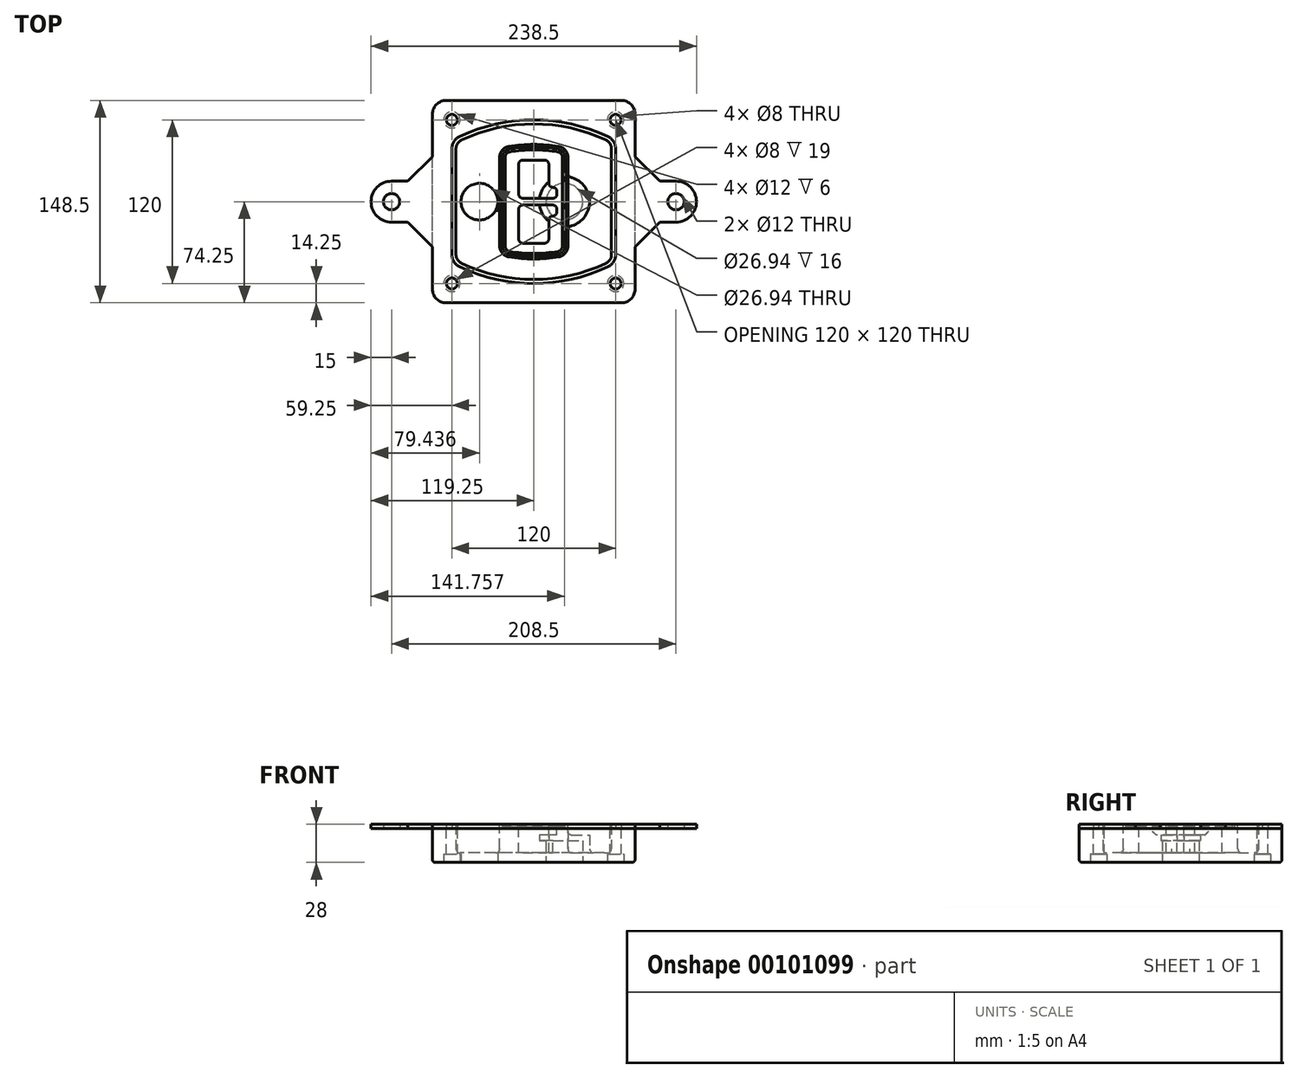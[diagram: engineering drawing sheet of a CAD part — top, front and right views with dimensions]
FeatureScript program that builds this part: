
annotation { "Feature Type Name" : "Feature", "Feature Type Description" : "" }
export const myFeature = defineFeature(function(context is Context, id is Id, definition is map)
    precondition{}
    {
        {
            var Q0;
            Q0=qCreatedBy(makeId("Top.planeOp"),FACE);
            var sketch = newSketch(context, id + "F0", { "sketchPlane" : qUnion([Q0])});
            skPoint(sketch, "E0.rect.middle", {"position": v(0, 0) * mm});
            skLineSegment(sketch, "E1.bottom", {"start": v(-64.25, -74.25) * mm, "end": v(64.25, -74.25) * mm});
            skLineSegment(sketch, "E1.top", {"start": v(-64.25, 74.25) * mm, "end": v(64.25, 74.25) * mm});
            skLineSegment(sketch, "E1.left", {"start": v(-74.25, -64.25) * mm, "end": v(-74.25, 64.25) * mm});
            skLineSegment(sketch, "E1.right", {"start": v(74.25, -64.25) * mm, "end": v(74.25, 64.25) * mm});
            skLineSegment(sketch, "E2", {"start": v(-74.25, 74.25) * mm, "end": v(74.25, -74.25) * mm, "construction": true});
            skLineSegment(sketch, "E3", {"start": v(74.25, 74.25) * mm, "end": v(-74.25, -74.25) * mm, "construction": true});
            skCircle(sketch, "E4", {"center": v(-60, 60) * mm, "radius": 4 * mm});
            skCircle(sketch, "E5", {"center": v(60, 60) * mm, "radius": 4 * mm});
            skCircle(sketch, "E6", {"center": v(60, -60) * mm, "radius": 4 * mm});
            skCircle(sketch, "E7", {"center": v(-60, -60) * mm, "radius": 4 * mm});
            skLineSegment(sketch, "E8", {"start": v(-60, 60) * mm, "end": v(60, 60) * mm, "construction": true});
            skLineSegment(sketch, "E9", {"start": v(60, 60) * mm, "end": v(60, -60) * mm, "construction": true});
            skLineSegment(sketch, "E10", {"start": v(60, -60) * mm, "end": v(-60, -60) * mm, "construction": true});
            skLineSegment(sketch, "E11", {"start": v(-60, -60) * mm, "end": v(-60, 60) * mm, "construction": true});
            skLineSegment(sketch, "E12", {"start": v(-60, 38.83) * mm, "end": v(-60, -38.83) * mm});
            skLineSegment(sketch, "E13", {"start": v(60, 38.83) * mm, "end": v(60, -38.83) * mm});
            skArc(sketch, "E14", {"start": v(54.26, 47.88) * mm, "mid": v(0, 60) * mm, "end": v(-54.26, 47.88) * mm});
            skArc(sketch, "E15", {"start": v(-54.26, -47.88) * mm, "mid": v(0, -60) * mm, "end": v(54.26, -47.88) * mm});
            skLineSegment(sketch, "E16", {"start": v(-60, 0) * mm, "end": v(60, 0) * mm, "construction": true});
            skPoint(sketch, "E17.visualSharp", {"position": v(-60, -45) * mm});
            skArc(sketch, "E17.filletArc", {"start": v(-60, -38.83) * mm, "mid": v(-58.44, -44.2) * mm, "end": v(-54.26, -47.88) * mm});
            skPoint(sketch, "E18.visualSharp", {"position": v(-60, 45) * mm});
            skArc(sketch, "E18.filletArc", {"start": v(-54.26, 47.88) * mm, "mid": v(-58.44, 44.2) * mm, "end": v(-60, 38.83) * mm});
            skPoint(sketch, "E19.visualSharp", {"position": v(60, 45) * mm});
            skArc(sketch, "E19.filletArc", {"start": v(60, 38.83) * mm, "mid": v(58.44, 44.2) * mm, "end": v(54.26, 47.88) * mm});
            skPoint(sketch, "E20.visualSharp", {"position": v(60, -45) * mm});
            skArc(sketch, "E20.filletArc", {"start": v(54.26, -47.88) * mm, "mid": v(58.44, -44.2) * mm, "end": v(60, -38.83) * mm});
            skPoint(sketch, "E21.visualSharp", {"position": v(-74.25, 74.25) * mm});
            skArc(sketch, "E21.filletArc", {"start": v(-64.25, 74.25) * mm, "mid": v(-71.32, 71.32) * mm, "end": v(-74.25, 64.25) * mm});
            skPoint(sketch, "E22.visualSharp", {"position": v(74.25, 74.25) * mm});
            skArc(sketch, "E22.filletArc", {"start": v(74.25, 64.25) * mm, "mid": v(71.32, 71.32) * mm, "end": v(64.25, 74.25) * mm});
            skPoint(sketch, "E23.visualSharp", {"position": v(74.25, -74.25) * mm});
            skArc(sketch, "E23.filletArc", {"start": v(64.25, -74.25) * mm, "mid": v(71.32, -71.32) * mm, "end": v(74.25, -64.25) * mm});
            skPoint(sketch, "E24.visualSharp", {"position": v(-74.25, -74.25) * mm});
            skArc(sketch, "E24.filletArc", {"start": v(-74.25, -64.25) * mm, "mid": v(-71.32, -71.32) * mm, "end": v(-64.25, -74.25) * mm});
            skArc(sketch, "E25.0", {"start": v(57, 38.83) * mm, "mid": v(55.9, 42.58) * mm, "end": v(52.98, 45.17) * mm});
            skLineSegment(sketch, "E25.1", {"start": v(57, 38.83) * mm, "end": v(57, -38.83) * mm});
            skArc(sketch, "E25.2", {"start": v(52.98, -45.17) * mm, "mid": v(55.9, -42.58) * mm, "end": v(57, -38.83) * mm});
            skArc(sketch, "E25.3", {"start": v(-52.98, -45.17) * mm, "mid": v(0, -57) * mm, "end": v(52.98, -45.17) * mm});
            skArc(sketch, "E25.4", {"start": v(-57, -38.83) * mm, "mid": v(-55.9, -42.58) * mm, "end": v(-52.98, -45.17) * mm});
            skArc(sketch, "E25.5", {"start": v(52.98, 45.17) * mm, "mid": v(0, 57) * mm, "end": v(-52.98, 45.17) * mm});
            skLineSegment(sketch, "E25.6", {"start": v(-57, 38.83) * mm, "end": v(-57, -38.83) * mm});
            skArc(sketch, "E25.7", {"start": v(-52.98, 45.17) * mm, "mid": v(-55.9, 42.58) * mm, "end": v(-57, 38.83) * mm});
            skArc(sketch, "E26.0", {"start": v(-55.96, 51.5) * mm, "mid": v(-61.82, 46.33) * mm, "end": v(-64, 38.83) * mm});
            skArc(sketch, "E26.1", {"start": v(55.96, 51.5) * mm, "mid": v(0, 64) * mm, "end": v(-55.96, 51.5) * mm});
            skArc(sketch, "E26.2", {"start": v(64, 38.83) * mm, "mid": v(61.82, 46.33) * mm, "end": v(55.96, 51.5) * mm});
            skLineSegment(sketch, "E26.3", {"start": v(64, 38.83) * mm, "end": v(64, -38.83) * mm});
            skArc(sketch, "E26.4", {"start": v(55.96, -51.5) * mm, "mid": v(61.82, -46.33) * mm, "end": v(64, -38.83) * mm});
            skLineSegment(sketch, "E26.5", {"start": v(-64, 38.83) * mm, "end": v(-64, -38.83) * mm});
            skArc(sketch, "E26.6", {"start": v(-55.96, -51.5) * mm, "mid": v(0, -64) * mm, "end": v(55.96, -51.5) * mm});
            skArc(sketch, "E26.7", {"start": v(-64, -38.83) * mm, "mid": v(-61.82, -46.33) * mm, "end": v(-55.96, -51.5) * mm});
            skSolve(sketch);
        }
        {
            var Q0;
            Q0=makeQuery(id+"F0.imprint","IMPRINT",FACE,{"disambiguationData":[TD([[makeQuery(id+"F0.imprint","IMPRINT",EDGE,{"derivedFrom":sQuery(id+"F0.wireOp",EDGE,"E1.bottom")}),1.0]])]});
            var Q1;
            Q1=makeQuery(id+"F0.imprint","IMPRINT",FACE,{"disambiguationData":[TD([[makeQuery(id+"F0.imprint","IMPRINT",EDGE,{"derivedFrom":sQuery(id+"F0.wireOp",EDGE,"E12")}),1.0]])]});
            var Q2;
            Q2=makeQuery(id+"F0.imprint","IMPRINT",FACE,{"disambiguationData":[TD([[makeQuery(id+"F0.imprint","IMPRINT",EDGE,{"derivedFrom":sQuery(id+"F0.wireOp",EDGE,"E25.0")}),1.0]])]});
            var Q3;
            Q3=makeQuery(id+"F0.imprint","IMPRINT",FACE,{"disambiguationData":[TD([[makeQuery(id+"F0.imprint","IMPRINT",EDGE,{"derivedFrom":sQuery(id+"F0.wireOp",EDGE,"E12")}),-1.0]])]});
            extrude(context, id + "F1", {"entities" : qUnion([Q0, Q1, Q2, Q3]), "oppositeDirection" : true, "depth" : 25 * mm});
        }
        {
            var Q0;
            Q0=makeQuery(id+"F0.imprint","IMPRINT",FACE,{"disambiguationData":[TD([[makeQuery(id+"F0.imprint","IMPRINT",EDGE,{"derivedFrom":sQuery(id+"F0.wireOp",EDGE,"E12")}),1.0]])]});
            extrude(context, id + "F2", {"entities" : qUnion([Q0]), "operationType" : NewBodyOperationType.ADD, "depth" : 3 * mm});
        }
        {
            var Q0;
            Q0=makeQuery(id+"F0.imprint","IMPRINT",FACE,{"disambiguationData":[TD([[makeQuery(id+"F0.imprint","IMPRINT",EDGE,{"derivedFrom":sQuery(id+"F0.wireOp",EDGE,"E25.0")}),1.0]])]});
            extrude(context, id + "F3", {"entities" : qUnion([Q0]), "operationType" : NewBodyOperationType.REMOVE, "oppositeDirection" : true, "depth" : 18 * mm});
        }
        {
            var Q0;
            Q0=makeQuery(id+"F2.opExtrude","CAP_FACE",FACE,{"disambiguationData":[OSD([sQuery(id+"F0.wireOp",EDGE,"E12"),sQuery(id+"F0.wireOp",EDGE,"E13"),sQuery(id+"F0.wireOp",EDGE,"E14"),sQuery(id+"F0.wireOp",EDGE,"E15"),sQuery(id+"F0.wireOp",EDGE,"E17.filletArc"),sQuery(id+"F0.wireOp",EDGE,"E18.filletArc"),sQuery(id+"F0.wireOp",EDGE,"E19.filletArc"),sQuery(id+"F0.wireOp",EDGE,"E20.filletArc"),sQuery(id+"F0.wireOp",EDGE,"E25.0"),sQuery(id+"F0.wireOp",EDGE,"E25.1"),sQuery(id+"F0.wireOp",EDGE,"E25.2"),sQuery(id+"F0.wireOp",EDGE,"E25.3"),sQuery(id+"F0.wireOp",EDGE,"E25.4"),sQuery(id+"F0.wireOp",EDGE,"E25.5"),sQuery(id+"F0.wireOp",EDGE,"E25.6"),sQuery(id+"F0.wireOp",EDGE,"E25.7")])],"isStart":false});
            var sketch = newSketch(context, id + "F4", { "sketchPlane" : qUnion([Q0])});
            skArc(sketch, "E27.0", {"start": v(-18.34, -40.45) * mm, "mid": v(0, -42) * mm, "end": v(18.34, -40.45) * mm});
            skArc(sketch, "E28.0", {"start": v(18.34, 40.45) * mm, "mid": v(0, 42) * mm, "end": v(-18.34, 40.45) * mm});
            skLineSegment(sketch, "E29", {"start": v(-25, 32.57) * mm, "end": v(-25, -32.57) * mm});
            skLineSegment(sketch, "E30", {"start": v(25, 32.57) * mm, "end": v(25, -32.57) * mm});
            skLineSegment(sketch, "E31", {"start": v(-25, 39.1) * mm, "end": v(25, 39.1) * mm, "construction": true});
            skLineSegment(sketch, "E32", {"start": v(-25, -39.1) * mm, "end": v(25, -39.1) * mm, "construction": true});
            skPoint(sketch, "E33.visualSharp", {"position": v(-25, 39.1) * mm});
            skArc(sketch, "E33.filletArc", {"start": v(-18.34, 40.45) * mm, "mid": v(-23.11, 37.73) * mm, "end": v(-25, 32.57) * mm});
            skPoint(sketch, "E34.visualSharp", {"position": v(25, 39.1) * mm});
            skArc(sketch, "E34.filletArc", {"start": v(25, 32.57) * mm, "mid": v(23.11, 37.73) * mm, "end": v(18.34, 40.45) * mm});
            skPoint(sketch, "E35.visualSharp", {"position": v(25, -39.1) * mm});
            skArc(sketch, "E35.filletArc", {"start": v(18.34, -40.45) * mm, "mid": v(23.11, -37.73) * mm, "end": v(25, -32.57) * mm});
            skPoint(sketch, "E36.visualSharp", {"position": v(-25, -39.1) * mm});
            skArc(sketch, "E36.filletArc", {"start": v(-25, -32.57) * mm, "mid": v(-23.11, -37.73) * mm, "end": v(-18.34, -40.45) * mm});
            skArc(sketch, "E37.0", {"start": v(52.98, 45.17) * mm, "mid": v(0, 57) * mm, "end": v(-52.98, 45.17) * mm});
            skArc(sketch, "E37.1", {"start": v(-52.98, 45.17) * mm, "mid": v(-55.9, 42.58) * mm, "end": v(-57, 38.83) * mm});
            skLineSegment(sketch, "E37.2", {"start": v(-57, 38.83) * mm, "end": v(-57, -38.83) * mm});
            skArc(sketch, "E37.3", {"start": v(-57, -38.83) * mm, "mid": v(-55.9, -42.58) * mm, "end": v(-52.98, -45.17) * mm});
            skArc(sketch, "E37.4", {"start": v(-52.98, -45.17) * mm, "mid": v(0, -57) * mm, "end": v(52.98, -45.17) * mm});
            skArc(sketch, "E37.5", {"start": v(52.98, -45.17) * mm, "mid": v(55.9, -42.58) * mm, "end": v(57, -38.83) * mm});
            skLineSegment(sketch, "E37.6", {"start": v(57, 38.83) * mm, "end": v(57, -38.83) * mm});
            skArc(sketch, "E37.7", {"start": v(57, 38.83) * mm, "mid": v(55.9, 42.58) * mm, "end": v(52.98, 45.17) * mm});
            skLineSegment(sketch, "E38.0", {"start": v(23, 32.57) * mm, "end": v(23, -32.57) * mm});
            skArc(sketch, "E38.1", {"start": v(18, -38.48) * mm, "mid": v(21.58, -36.44) * mm, "end": v(23, -32.57) * mm});
            skArc(sketch, "E38.2", {"start": v(-18, -38.48) * mm, "mid": v(0, -40) * mm, "end": v(18, -38.48) * mm});
            skArc(sketch, "E38.3", {"start": v(-23, -32.57) * mm, "mid": v(-21.58, -36.44) * mm, "end": v(-18, -38.48) * mm});
            skLineSegment(sketch, "E38.4", {"start": v(-23, 32.57) * mm, "end": v(-23, -32.57) * mm});
            skArc(sketch, "E38.5", {"start": v(23, 32.57) * mm, "mid": v(21.58, 36.44) * mm, "end": v(18, 38.48) * mm});
            skArc(sketch, "E38.6", {"start": v(-18, 38.48) * mm, "mid": v(-21.58, 36.44) * mm, "end": v(-23, 32.57) * mm});
            skArc(sketch, "E38.7", {"start": v(18, 38.48) * mm, "mid": v(0, 40) * mm, "end": v(-18, 38.48) * mm});
            skArc(sketch, "E39.0", {"start": v(21, 32.57) * mm, "mid": v(20.06, 35.15) * mm, "end": v(17.67, 36.5) * mm});
            skLineSegment(sketch, "E39.1", {"start": v(21, 32.57) * mm, "end": v(21, -32.57) * mm});
            skArc(sketch, "E39.2", {"start": v(17.67, -36.5) * mm, "mid": v(20.06, -35.15) * mm, "end": v(21, -32.57) * mm});
            skArc(sketch, "E39.3", {"start": v(-17.67, -36.5) * mm, "mid": v(0, -38) * mm, "end": v(17.67, -36.5) * mm});
            skArc(sketch, "E39.4", {"start": v(-21, -32.57) * mm, "mid": v(-20.06, -35.15) * mm, "end": v(-17.67, -36.5) * mm});
            skArc(sketch, "E39.5", {"start": v(17.67, 36.5) * mm, "mid": v(0, 38) * mm, "end": v(-17.67, 36.5) * mm});
            skLineSegment(sketch, "E39.6", {"start": v(-21, 32.57) * mm, "end": v(-21, -32.57) * mm});
            skArc(sketch, "E39.7", {"start": v(-17.67, 36.5) * mm, "mid": v(-20.06, 35.15) * mm, "end": v(-21, 32.57) * mm});
            skLineSegment(sketch, "E40", {"start": v(-25, 0) * mm, "end": v(25, 0) * mm, "construction": true});
            skLineSegment(sketch, "E41", {"start": v(-11, 5.5) * mm, "end": v(-11, 27.5) * mm});
            skLineSegment(sketch, "E42", {"start": v(-8, 30.5) * mm, "end": v(8, 30.5) * mm});
            skLineSegment(sketch, "E43", {"start": v(11, 27.5) * mm, "end": v(11, 13.5) * mm});
            skLineSegment(sketch, "E44", {"start": v(14, 10.5) * mm, "end": v(14, 10.5) * mm});
            skLineSegment(sketch, "E45", {"start": v(17, 7.5) * mm, "end": v(17, 5.5) * mm});
            skLineSegment(sketch, "E46", {"start": v(14, 2.5) * mm, "end": v(-8, 2.5) * mm});
            skPoint(sketch, "E47.visualSharp", {"position": v(-11, 30.5) * mm});
            skArc(sketch, "E47.filletArc", {"start": v(-8, 30.5) * mm, "mid": v(-10.12, 29.62) * mm, "end": v(-11, 27.5) * mm});
            skPoint(sketch, "E48.visualSharp", {"position": v(11, 30.5) * mm});
            skArc(sketch, "E48.filletArc", {"start": v(11, 27.5) * mm, "mid": v(10.12, 29.62) * mm, "end": v(8, 30.5) * mm});
            skPoint(sketch, "E49.visualSharp", {"position": v(11, 10.5) * mm});
            skArc(sketch, "E49.filletArc", {"start": v(11, 13.5) * mm, "mid": v(11.88, 11.38) * mm, "end": v(14, 10.5) * mm});
            skPoint(sketch, "E50.visualSharp", {"position": v(17, 10.5) * mm});
            skArc(sketch, "E50.filletArc", {"start": v(17, 7.5) * mm, "mid": v(16.12, 9.62) * mm, "end": v(14, 10.5) * mm});
            skPoint(sketch, "E51.visualSharp", {"position": v(17, 2.5) * mm});
            skArc(sketch, "E51.filletArc", {"start": v(14, 2.5) * mm, "mid": v(16.12, 3.38) * mm, "end": v(17, 5.5) * mm});
            skPoint(sketch, "E52.visualSharp", {"position": v(-11, 2.5) * mm});
            skArc(sketch, "E52.filletArc", {"start": v(-11, 5.5) * mm, "mid": v(-10.12, 3.38) * mm, "end": v(-8, 2.5) * mm});
            skLineSegment(sketch, "E53.0.MirrorCS", {"start": v(14, -2.5) * mm, "end": v(-8, -2.5) * mm});
            skArc(sketch, "E54.0.MirrorCS", {"start": v(-11, -5.5) * mm, "mid": v(-10.12, -3.38) * mm, "end": v(-8, -2.5) * mm});
            skLineSegment(sketch, "E55.0.MirrorCS", {"start": v(-11, -5.5) * mm, "end": v(-11, -27.5) * mm});
            skArc(sketch, "E56.0.MirrorCS", {"start": v(-8, -30.5) * mm, "mid": v(-10.12, -29.62) * mm, "end": v(-11, -27.5) * mm});
            skLineSegment(sketch, "E57.0.MirrorCS", {"start": v(-8, -30.5) * mm, "end": v(8, -30.5) * mm});
            skArc(sketch, "E58.0.MirrorCS", {"start": v(11, -27.5) * mm, "mid": v(10.12, -29.62) * mm, "end": v(8, -30.5) * mm});
            skLineSegment(sketch, "E59.0.MirrorCS", {"start": v(11, -27.5) * mm, "end": v(11, -13.5) * mm});
            skArc(sketch, "E60.0.MirrorCS", {"start": v(11, -13.5) * mm, "mid": v(11.88, -11.38) * mm, "end": v(14, -10.5) * mm});
            skArc(sketch, "E61.0.MirrorCS", {"start": v(17, -7.5) * mm, "mid": v(16.12, -9.62) * mm, "end": v(14, -10.5) * mm});
            skLineSegment(sketch, "E62.0.MirrorCS", {"start": v(17, -7.5) * mm, "end": v(17, -5.5) * mm});
            skArc(sketch, "E63.0.MirrorCS", {"start": v(14, -2.5) * mm, "mid": v(16.12, -3.38) * mm, "end": v(17, -5.5) * mm});
            skSolve(sketch);
        }
        {
            var Q0;
            Q0=makeQuery(id+"F4.imprint","IMPRINT",FACE,{"disambiguationData":[TD([[makeQuery(id+"F4.imprint","IMPRINT",EDGE,{"derivedFrom":sQuery(id+"F4.wireOp",EDGE,"E27.0")}),1.0]])]});
            var Q1;
            Q1=makeQuery(id+"F4.imprint","IMPRINT",FACE,{"disambiguationData":[TD([[makeQuery(id+"F4.imprint","IMPRINT",EDGE,{"derivedFrom":sQuery(id+"F4.wireOp",EDGE,"E38.0")}),-1.0]])]});
            var Q2;
            Q2=makeQuery(id+"F4.imprint","IMPRINT",FACE,{"disambiguationData":[TD([[makeQuery(id+"F4.imprint","IMPRINT",EDGE,{"derivedFrom":sQuery(id+"F4.wireOp",EDGE,"E39.0")}),1.0]])]});
            extrude(context, id + "F5", {"entities" : qUnion([Q0, Q1, Q2]), "operationType" : NewBodyOperationType.ADD, "endBound" : BoundingType.UP_TO_NEXT, "oppositeDirection" : true, "depth" : 25 * mm});
        }
        {
            var Q0;
            Q0=makeQuery(id+"F4.imprint","IMPRINT",FACE,{"disambiguationData":[TD([[makeQuery(id+"F4.imprint","IMPRINT",EDGE,{"derivedFrom":sQuery(id+"F4.wireOp",EDGE,"E38.0")}),-1.0]])]});
            extrude(context, id + "F6", {"entities" : qUnion([Q0]), "operationType" : NewBodyOperationType.REMOVE, "oppositeDirection" : true, "depth" : 2 * mm});
        }
        {
            var Q0;
            Q0=makeQuery(id+"F1.opExtrude","CAP_FACE",FACE,{"disambiguationData":[OSD([sQuery(id+"F0.wireOp",EDGE,"E1.bottom"),sQuery(id+"F0.wireOp",EDGE,"E1.top"),sQuery(id+"F0.wireOp",EDGE,"E1.left"),sQuery(id+"F0.wireOp",EDGE,"E1.right"),sQuery(id+"F0.wireOp",EDGE,"E4"),sQuery(id+"F0.wireOp",EDGE,"E5"),sQuery(id+"F0.wireOp",EDGE,"E6"),sQuery(id+"F0.wireOp",EDGE,"E7"),sQuery(id+"F0.wireOp",EDGE,"E21.filletArc"),sQuery(id+"F0.wireOp",EDGE,"E22.filletArc"),sQuery(id+"F0.wireOp",EDGE,"E23.filletArc"),sQuery(id+"F0.wireOp",EDGE,"E24.filletArc")])],"isStart":false});
            var sketch = newSketch(context, id + "F7", { "sketchPlane" : qUnion([Q0])});
            skCircle(sketch, "E64", {"center": v(22.5, 0) * mm, "radius": 13.47 * mm});
            skCircle(sketch, "E65", {"center": v(-39.81, 0) * mm, "radius": 13.47 * mm});
            skLineSegment(sketch, "E66", {"start": v(74.25, 0) * mm, "end": v(-74.25, 0) * mm});
            skCircle(sketch, "E67", {"center": v(22.5, 0) * mm, "radius": 18.47 * mm});
            skCircle(sketch, "E68", {"center": v(60, -60) * mm, "radius": 6 * mm});
            skCircle(sketch, "E69", {"center": v(-60, -60) * mm, "radius": 6 * mm});
            skCircle(sketch, "E70", {"center": v(-60, 60) * mm, "radius": 6 * mm});
            skCircle(sketch, "E71", {"center": v(60, 60) * mm, "radius": 6 * mm});
            skSolve(sketch);
        }
        {
            var Q0;
            {var subQ1=sQuery(id+"F7.wireOp",EDGE,"E66");var subQ4=sQuery(id+"F7.wireOp",EDGE,"E64");var subQ6=makeQuery(id+"F7.imprint","INTERSECT",VERTEX,{"disambiguationData":[OD(0.0)],"derivedFrom":[subQ4,subQ1]});Q0=makeQuery(id+"F7.imprint","IMPRINT",FACE,{"disambiguationData":[TD([[makeQuery(id+"F7.imprint","IMPRINT",EDGE,{"disambiguationData":[TD([[subQ6,-1.0]])],"derivedFrom":subQ4}),-1.0]])]});}
            var Q1;
            {var subQ0=sQuery(id+"F7.wireOp",EDGE,"E66");var subQ1=sQuery(id+"F7.wireOp",EDGE,"E64");var subQ3=makeQuery(id+"F7.imprint","INTERSECT",VERTEX,{"disambiguationData":[OD(0.0)],"derivedFrom":[subQ1,subQ0]});Q1=makeQuery(id+"F7.imprint","IMPRINT",FACE,{"disambiguationData":[TD([[makeQuery(id+"F7.imprint","IMPRINT",EDGE,{"disambiguationData":[TD([[subQ3,-1.0]])],"derivedFrom":subQ1}),1.0]])]});}
            var Q2;
            {var subQ0=sQuery(id+"F7.wireOp",EDGE,"E66");var subQ1=sQuery(id+"F7.wireOp",EDGE,"E64");var subQ3=makeQuery(id+"F7.imprint","INTERSECT",VERTEX,{"disambiguationData":[OD(0.0)],"derivedFrom":[subQ1,subQ0]});Q2=makeQuery(id+"F7.imprint","IMPRINT",FACE,{"disambiguationData":[TD([[makeQuery(id+"F7.imprint","IMPRINT",EDGE,{"disambiguationData":[TD([[subQ3,1.0]])],"derivedFrom":subQ1}),1.0]])]});}
            var Q3;
            {var subQ1=sQuery(id+"F7.wireOp",EDGE,"E66");var subQ4=sQuery(id+"F7.wireOp",EDGE,"E64");var subQ6=makeQuery(id+"F7.imprint","INTERSECT",VERTEX,{"disambiguationData":[OD(0.0)],"derivedFrom":[subQ4,subQ1]});Q3=makeQuery(id+"F7.imprint","IMPRINT",FACE,{"disambiguationData":[TD([[makeQuery(id+"F7.imprint","IMPRINT",EDGE,{"disambiguationData":[TD([[subQ6,1.0]])],"derivedFrom":subQ4}),-1.0]])]});}
            extrude(context, id + "F8", {"entities" : qUnion([Q0, Q1, Q2, Q3]), "operationType" : NewBodyOperationType.ADD, "oppositeDirection" : true, "depth" : 20 * mm});
        }
        {
            var Q0;
            {var subQ0=sQuery(id+"F7.wireOp",EDGE,"E66");var subQ1=sQuery(id+"F7.wireOp",EDGE,"E64");var subQ3=makeQuery(id+"F7.imprint","INTERSECT",VERTEX,{"disambiguationData":[OD(0.0)],"derivedFrom":[subQ1,subQ0]});Q0=makeQuery(id+"F7.imprint","IMPRINT",FACE,{"disambiguationData":[TD([[makeQuery(id+"F7.imprint","IMPRINT",EDGE,{"disambiguationData":[TD([[subQ3,-1.0]])],"derivedFrom":subQ1}),1.0]])]});}
            var Q1;
            {var subQ0=sQuery(id+"F7.wireOp",EDGE,"E66");var subQ1=sQuery(id+"F7.wireOp",EDGE,"E64");var subQ3=makeQuery(id+"F7.imprint","INTERSECT",VERTEX,{"disambiguationData":[OD(0.0)],"derivedFrom":[subQ1,subQ0]});Q1=makeQuery(id+"F7.imprint","IMPRINT",FACE,{"disambiguationData":[TD([[makeQuery(id+"F7.imprint","IMPRINT",EDGE,{"disambiguationData":[TD([[subQ3,1.0]])],"derivedFrom":subQ1}),1.0]])]});}
            extrude(context, id + "F9", {"entities" : qUnion([Q0, Q1]), "operationType" : NewBodyOperationType.REMOVE, "oppositeDirection" : true, "depth" : 16 * mm});
        }
        {
            var Q0;
            {var subQ0=sQuery(id+"F7.wireOp",EDGE,"E66");var subQ1=sQuery(id+"F7.wireOp",EDGE,"E65");var subQ3=makeQuery(id+"F7.imprint","INTERSECT",VERTEX,{"disambiguationData":[OD(0.0)],"derivedFrom":[subQ1,subQ0]});Q0=makeQuery(id+"F7.imprint","IMPRINT",FACE,{"disambiguationData":[TD([[makeQuery(id+"F7.imprint","IMPRINT",EDGE,{"disambiguationData":[TD([[subQ3,-1.0]])],"derivedFrom":subQ1}),1.0]])]});}
            var Q1;
            {var subQ0=sQuery(id+"F7.wireOp",EDGE,"E66");var subQ1=sQuery(id+"F7.wireOp",EDGE,"E65");var subQ3=makeQuery(id+"F7.imprint","INTERSECT",VERTEX,{"disambiguationData":[OD(0.0)],"derivedFrom":[subQ1,subQ0]});Q1=makeQuery(id+"F7.imprint","IMPRINT",FACE,{"disambiguationData":[TD([[makeQuery(id+"F7.imprint","IMPRINT",EDGE,{"disambiguationData":[TD([[subQ3,1.0]])],"derivedFrom":subQ1}),1.0]])]});}
            extrude(context, id + "F10", {"entities" : qUnion([Q0, Q1]), "operationType" : NewBodyOperationType.REMOVE, "oppositeDirection" : true, "depth" : 25 * mm});
        }
        {
            var Q0;
            Q0=makeQuery(id+"F7.imprint","IMPRINT",FACE,{"disambiguationData":[TD([[makeQuery(id+"F7.imprint","IMPRINT",EDGE,{"derivedFrom":sQuery(id+"F7.wireOp",EDGE,"E68")}),1.0]])]});
            var Q1;
            Q1=makeQuery(id+"F7.imprint","IMPRINT",FACE,{"disambiguationData":[TD([[makeQuery(id+"F7.imprint","IMPRINT",EDGE,{"derivedFrom":makeQuery(id+"F1.opExtrude","CAP_EDGE",EDGE,{"disambiguationData":[OSD([sQuery(id+"F0.wireOp",EDGE,"E5")])],"isStart":false})}),-1.0]])]});
            var Q2;
            Q2=makeQuery(id+"F7.imprint","IMPRINT",FACE,{"disambiguationData":[TD([[makeQuery(id+"F7.imprint","IMPRINT",EDGE,{"derivedFrom":sQuery(id+"F7.wireOp",EDGE,"E69")}),1.0]])]});
            var Q3;
            Q3=makeQuery(id+"F7.imprint","IMPRINT",FACE,{"disambiguationData":[TD([[makeQuery(id+"F7.imprint","IMPRINT",EDGE,{"derivedFrom":makeQuery(id+"F1.opExtrude","CAP_EDGE",EDGE,{"disambiguationData":[OSD([sQuery(id+"F0.wireOp",EDGE,"E4")])],"isStart":false})}),-1.0]])]});
            var Q4;
            Q4=makeQuery(id+"F7.imprint","IMPRINT",FACE,{"disambiguationData":[TD([[makeQuery(id+"F7.imprint","IMPRINT",EDGE,{"derivedFrom":sQuery(id+"F7.wireOp",EDGE,"E70")}),1.0]])]});
            var Q5;
            Q5=makeQuery(id+"F7.imprint","IMPRINT",FACE,{"disambiguationData":[TD([[makeQuery(id+"F7.imprint","IMPRINT",EDGE,{"derivedFrom":makeQuery(id+"F1.opExtrude","CAP_EDGE",EDGE,{"disambiguationData":[OSD([sQuery(id+"F0.wireOp",EDGE,"E7")])],"isStart":false})}),-1.0]])]});
            var Q6;
            Q6=makeQuery(id+"F7.imprint","IMPRINT",FACE,{"disambiguationData":[TD([[makeQuery(id+"F7.imprint","IMPRINT",EDGE,{"derivedFrom":sQuery(id+"F7.wireOp",EDGE,"E71")}),1.0]])]});
            var Q7;
            Q7=makeQuery(id+"F7.imprint","IMPRINT",FACE,{"disambiguationData":[TD([[makeQuery(id+"F7.imprint","IMPRINT",EDGE,{"derivedFrom":makeQuery(id+"F1.opExtrude","CAP_EDGE",EDGE,{"disambiguationData":[OSD([sQuery(id+"F0.wireOp",EDGE,"E6")])],"isStart":false})}),-1.0]])]});
            extrude(context, id + "F11", {"entities" : qUnion([Q0, Q1, Q2, Q3, Q4, Q5, Q6, Q7]), "operationType" : NewBodyOperationType.REMOVE, "oppositeDirection" : true, "depth" : 6 * mm});
        }
        {
            var Q0;
            Q0=makeQuery(id+"F9.boolean.opBoolean","COPY",FACE,{"derivedFrom":makeQuery(id+"F9.opExtrude","CAP_FACE",FACE,{"disambiguationData":[OSD([sQuery(id+"F7.wireOp",EDGE,"E64")])],"isStart":false})});
            var sketch = newSketch(context, id + "F12", { "sketchPlane" : qUnion([Q0])});
            skArc(sketch, "E72.0", {"start": v(11, 14.45) * mm, "mid": v(6.45, 9.13) * mm, "end": v(4.2, 2.5) * mm});
            skArc(sketch, "E72.1", {"start": v(4.2, -2.5) * mm, "mid": v(6.45, -9.13) * mm, "end": v(11, -14.45) * mm});
            skLineSegment(sketch, "E73", {"start": v(4.2, -2.5) * mm, "end": v(14, -2.5) * mm});
            skLineSegment(sketch, "E74.0", {"start": v(14, 2.5) * mm, "end": v(4.2, 2.5) * mm});
            skArc(sketch, "E74.1", {"start": v(14, 2.5) * mm, "mid": v(16.12, 3.38) * mm, "end": v(17, 5.5) * mm});
            skLineSegment(sketch, "E74.2", {"start": v(17, 7.5) * mm, "end": v(17, 5.5) * mm});
            skArc(sketch, "E74.3", {"start": v(17, 7.5) * mm, "mid": v(16.12, 9.62) * mm, "end": v(14, 10.5) * mm});
            skArc(sketch, "E74.4", {"start": v(11, 13.5) * mm, "mid": v(11.88, 11.38) * mm, "end": v(14, 10.5) * mm});
            skLineSegment(sketch, "E74.5", {"start": v(11, 14.45) * mm, "end": v(11, 13.5) * mm});
            skLineSegment(sketch, "E74.7", {"start": v(14, -2.5) * mm, "end": v(4.2, -2.5) * mm});
            skArc(sketch, "E74.8", {"start": v(14, -2.5) * mm, "mid": v(16.12, -3.38) * mm, "end": v(17, -5.5) * mm});
            skLineSegment(sketch, "E74.9", {"start": v(17, -7.5) * mm, "end": v(17, -5.5) * mm});
            skArc(sketch, "E74.10", {"start": v(17, -7.5) * mm, "mid": v(16.12, -9.62) * mm, "end": v(14, -10.5) * mm});
            skArc(sketch, "E74.11", {"start": v(11, -13.5) * mm, "mid": v(11.88, -11.38) * mm, "end": v(14, -10.5) * mm});
            skLineSegment(sketch, "E74.12", {"start": v(11, -14.45) * mm, "end": v(11, -13.5) * mm});
            skPoint(sketch, "E75.orphan", {"position": v(11, -27.5) * mm});
            skPoint(sketch, "E76.orphan", {"position": v(-8, -2.5) * mm});
            skPoint(sketch, "E77.orphan", {"position": v(-8, 2.5) * mm});
            skPoint(sketch, "E78.orphan", {"position": v(11, 27.5) * mm});
            skSolve(sketch);
        }
        {
            var Q0;
            {var subQ7=sQuery(id+"F12.wireOp",EDGE,"E72.0");var subQ14=sQuery(id+"F12.wireOp",EDGE,"E72.1");var subQ16=sQuery(id+"F12.wireOp",EDGE,"E74.1");var subQ18=sQuery(id+"F12.wireOp",EDGE,"E74.8");Q0=qUnion([makeQuery(id+"F12.imprint","IMPRINT",FACE,{"disambiguationData":[TD([[makeQuery(id+"F12.imprint","IMPRINT",EDGE,{"derivedFrom":subQ7}),1.0]])]}),makeQuery(id+"F12.imprint","IMPRINT",FACE,{"disambiguationData":[TD([[makeQuery(id+"F12.imprint","IMPRINT",EDGE,{"derivedFrom":subQ14}),1.0]])]}),makeQuery(id+"F12.imprint","IMPRINT",FACE,{"disambiguationData":[TD([[makeQuery(id+"F12.imprint","IMPRINT",EDGE,{"derivedFrom":subQ16}),1.0]])]}),makeQuery(id+"F12.imprint","IMPRINT",FACE,{"disambiguationData":[TD([[makeQuery(id+"F12.imprint","IMPRINT",EDGE,{"derivedFrom":subQ18}),-1.0]])]})]);}
            var Q1;
            Q1=makeQuery(id+"F5.boolean.opBoolean","SPLIT",FACE,{"disambiguationData":[TD([makeQuery(id+"F5.opExtrude","SWEPT_FACE",FACE,{"disambiguationData":[OSD([sQuery(id+"F4.wireOp",EDGE,"E41")])]})])],"derivedFrom":makeQuery(id+"F3.boolean.opBoolean","COPY",FACE,{"derivedFrom":makeQuery(id+"F3.opExtrude","CAP_FACE",FACE,{"disambiguationData":[OSD([sQuery(id+"F0.wireOp",EDGE,"E25.0"),sQuery(id+"F0.wireOp",EDGE,"E25.1"),sQuery(id+"F0.wireOp",EDGE,"E25.2"),sQuery(id+"F0.wireOp",EDGE,"E25.3"),sQuery(id+"F0.wireOp",EDGE,"E25.4"),sQuery(id+"F0.wireOp",EDGE,"E25.5"),sQuery(id+"F0.wireOp",EDGE,"E25.6"),sQuery(id+"F0.wireOp",EDGE,"E25.7")])],"isStart":false})})});
            extrude(context, id + "F13", {"entities" : qUnion([Q0]), "operationType" : NewBodyOperationType.REMOVE, "endBound" : BoundingType.UP_TO_SURFACE, "endBoundEntityFace" : qUnion([Q1]), "depth" : 25 * mm});
        }
        {
            var Q0;
            Q0=makeQuery(id+"F3.boolean.opBoolean","COPY",EDGE,{"derivedFrom":makeQuery(id+"F3.opExtrude","CAP_EDGE",EDGE,{"disambiguationData":[OSD([sQuery(id+"F0.wireOp",EDGE,"E25.6")])],"isStart":false})});
            var Q1;
            Q1=makeQuery(id+"F8.boolean.opBoolean","INTERSECT",EDGE,{"derivedFrom":[makeQuery(id+"F5.opExtrude","SWEPT_FACE",FACE,{"disambiguationData":[OSD([sQuery(id+"F4.wireOp",EDGE,"E30")])]}),makeQuery(id+"F8.opExtrude","CAP_FACE",FACE,{"disambiguationData":[OSD([sQuery(id+"F7.wireOp",EDGE,"E67")])],"isStart":false})]});
            var Q2;
            Q2=makeQuery(id+"F8.boolean.opBoolean","INTERSECT",EDGE,{"disambiguationData":[OD(1.0)],"derivedFrom":[makeQuery(id+"F5.opExtrude","SWEPT_FACE",FACE,{"disambiguationData":[OSD([sQuery(id+"F4.wireOp",EDGE,"E30")])]}),makeQuery(id+"F8.opExtrude","SWEPT_FACE",FACE,{"disambiguationData":[OSD([sQuery(id+"F7.wireOp",EDGE,"E67")])]})]});
            var Q3;
            {var subQ0=sQuery(id+"F4.wireOp",EDGE,"E30");Q3=makeQuery(id+"F8.boolean.opBoolean","SPLIT",EDGE,{"disambiguationData":[TD([makeQuery(id+"F5.opExtrude","SWEPT_FACE",FACE,{"disambiguationData":[OSD([sQuery(id+"F4.wireOp",EDGE,"E35.filletArc")])]})])],"derivedFrom":makeQuery(id+"F5.opExtrude","CAP_EDGE",EDGE,{"disambiguationData":[OSD([subQ0])],"isStart":false})});}
            var Q4;
            {var subQ0=sQuery(id+"F0.wireOp",EDGE,"E25.7");var subQ1=sQuery(id+"F0.wireOp",EDGE,"E25.1");var subQ2=sQuery(id+"F0.wireOp",EDGE,"E25.6");var subQ3=sQuery(id+"F0.wireOp",EDGE,"E25.5");var subQ4=sQuery(id+"F0.wireOp",EDGE,"E25.4");var subQ5=sQuery(id+"F0.wireOp",EDGE,"E25.0");var subQ6=sQuery(id+"F0.wireOp",EDGE,"E25.2");var subQ7=sQuery(id+"F0.wireOp",EDGE,"E25.3");Q4=makeQuery(id+"F8.boolean.opBoolean","INTERSECT",EDGE,{"derivedFrom":[makeQuery(id+"F5.boolean.opBoolean","SPLIT",FACE,{"disambiguationData":[TD([makeQuery(id+"F2.opExtrude","SWEPT_FACE",FACE,{"disambiguationData":[OSD([subQ5])]})])],"derivedFrom":makeQuery(id+"F3.boolean.opBoolean","COPY",FACE,{"derivedFrom":makeQuery(id+"F3.opExtrude","CAP_FACE",FACE,{"disambiguationData":[OSD([subQ5,subQ1,subQ6,subQ7,subQ4,subQ3,subQ2,subQ0])],"isStart":false})})}),makeQuery(id+"F8.opExtrude","SWEPT_FACE",FACE,{"disambiguationData":[OSD([sQuery(id+"F7.wireOp",EDGE,"E67")])]})]});}
            var Q5;
            Q5=makeQuery(id+"F8.boolean.opBoolean","INTERSECT",EDGE,{"disambiguationData":[OD(0.0)],"derivedFrom":[makeQuery(id+"F5.opExtrude","SWEPT_FACE",FACE,{"disambiguationData":[OSD([sQuery(id+"F4.wireOp",EDGE,"E30")])]}),makeQuery(id+"F8.opExtrude","SWEPT_FACE",FACE,{"disambiguationData":[OSD([sQuery(id+"F7.wireOp",EDGE,"E67")])]})]});
            fillet(context, id + "F14", {"entities" : qUnion([Q0, Q1, Q2, Q3, Q4, Q5]), "radius" : 3 * mm, "tangentPropagation" : true, "allowEdgeOverflow" : false});
        }
        {
            var Q0;
            Q0=makeQuery(id+"F1.opExtrude","CAP_EDGE",EDGE,{"disambiguationData":[OSD([sQuery(id+"F0.wireOp",EDGE,"E1.bottom")])],"isStart":false});
            fillet(context, id + "F15", {"entities" : qUnion([Q0]), "radius" : 2 * mm, "tangentPropagation" : true, "allowEdgeOverflow" : false});
        }
        {
            var Q0;
            {var subQ0=sQuery(id+"F0.wireOp",EDGE,"E22.filletArc");var subQ1=sQuery(id+"F0.wireOp",EDGE,"E7");var subQ2=sQuery(id+"F0.wireOp",EDGE,"E6");var subQ3=sQuery(id+"F0.wireOp",EDGE,"E5");var subQ4=sQuery(id+"F0.wireOp",EDGE,"E4");var subQ5=sQuery(id+"F0.wireOp",EDGE,"E1.bottom");var subQ6=sQuery(id+"F0.wireOp",EDGE,"E21.filletArc");var subQ7=sQuery(id+"F0.wireOp",EDGE,"E1.top");var subQ8=sQuery(id+"F0.wireOp",EDGE,"E1.left");var subQ9=sQuery(id+"F0.wireOp",EDGE,"E1.right");var subQ10=sQuery(id+"F0.wireOp",EDGE,"E23.filletArc");var subQ11=sQuery(id+"F0.wireOp",EDGE,"E24.filletArc");Q0=makeQuery(id+"F2.boolean.opBoolean","SPLIT",FACE,{"disambiguationData":[TD([makeQuery(id+"F1.opExtrude","SWEPT_FACE",FACE,{"disambiguationData":[OSD([subQ5])]})])],"derivedFrom":makeQuery(id+"F1.opExtrude","CAP_FACE",FACE,{"disambiguationData":[OSD([subQ5,subQ7,subQ8,subQ9,subQ4,subQ3,subQ2,subQ1,subQ6,subQ0,subQ10,subQ11])],"isStart":true})});}
            var sketch = newSketch(context, id + "F16", { "sketchPlane" : qUnion([Q0])});
            skPoint(sketch, "E79.endSnap0", {"position": v(74.25, 0) * mm});
            skLineSegment(sketch, "E80", {"start": v(74.25, 33) * mm, "end": v(92.25, 15) * mm});
            skLineSegment(sketch, "E81", {"start": v(92.25, 15) * mm, "end": v(104.25, 15) * mm});
            skArc(sketch, "E82", {"start": v(104.25, -15) * mm, "mid": v(119.25, 0) * mm, "end": v(104.25, 15) * mm});
            skLineSegment(sketch, "E83", {"start": v(104.25, -15) * mm, "end": v(92.25, -15) * mm});
            skLineSegment(sketch, "E84", {"start": v(92.25, -15) * mm, "end": v(74.25, -33) * mm});
            skLineSegment(sketch, "E85", {"start": v(74.25, 0) * mm, "end": v(104.25, 0) * mm, "construction": true});
            skCircle(sketch, "E86", {"center": v(104.25, 0) * mm, "radius": 6 * mm});
            skLineSegment(sketch, "E87", {"start": v(0, 74.25) * mm, "end": v(0, -74.25) * mm, "construction": true});
            skLineSegment(sketch, "E88.MirrorCS", {"start": v(-92.25, 15) * mm, "end": v(-104.25, 15) * mm});
            skCircle(sketch, "E89.MirrorC", {"center": v(-104.25, 0) * mm, "radius": 6 * mm});
            skLineSegment(sketch, "E90.MirrorCS", {"start": v(-74.25, 0) * mm, "end": v(-104.25, 0) * mm, "construction": true});
            skArc(sketch, "E91.MirrorCS", {"start": v(-104.25, -15) * mm, "mid": v(-119.25, 0) * mm, "end": v(-104.25, 15) * mm});
            skLineSegment(sketch, "E92.MirrorCS", {"start": v(-104.25, -15) * mm, "end": v(-92.25, -15) * mm});
            skLineSegment(sketch, "E93.MirrorCS", {"start": v(-92.25, -15) * mm, "end": v(-74.25, -33) * mm});
            skLineSegment(sketch, "E94.MirrorCS", {"start": v(-74.25, 33) * mm, "end": v(-92.25, 15) * mm});
            skPoint(sketch, "E95.MirrorP", {"position": v(-74.25, 0) * mm});
            skSolve(sketch);
        }
        {
            var Q0;
            Q0=makeQuery(id+"F16.imprint","IMPRINT",FACE,{"disambiguationData":[TD([[makeQuery(id+"F16.imprint","IMPRINT",EDGE,{"derivedFrom":sQuery(id+"F16.wireOp",EDGE,"E88.MirrorCS")}),1.0]])]});
            var Q1;
            Q1=makeQuery(id+"F16.imprint","IMPRINT",FACE,{"disambiguationData":[TD([[makeQuery(id+"F16.imprint","IMPRINT",EDGE,{"derivedFrom":makeQuery(id+"F1.opExtrude","CAP_EDGE",EDGE,{"disambiguationData":[OSD([sQuery(id+"F0.wireOp",EDGE,"E1.bottom")])],"isStart":true})}),1.0]])]});
            var Q2;
            {var subQ0=sQuery(id+"F16.wireOp",EDGE,"E80");Q2=makeQuery(id+"F16.imprint","IMPRINT",FACE,{"disambiguationData":[TD([[makeQuery(id+"F16.imprint","IMPRINT",EDGE,{"derivedFrom":subQ0}),-1.0]])]});}
            var Q3;
            Q3=makeQuery(id+"F2.opExtrude","CAP_FACE",FACE,{"disambiguationData":[OSD([sQuery(id+"F0.wireOp",EDGE,"E12"),sQuery(id+"F0.wireOp",EDGE,"E13"),sQuery(id+"F0.wireOp",EDGE,"E14"),sQuery(id+"F0.wireOp",EDGE,"E15"),sQuery(id+"F0.wireOp",EDGE,"E17.filletArc"),sQuery(id+"F0.wireOp",EDGE,"E18.filletArc"),sQuery(id+"F0.wireOp",EDGE,"E19.filletArc"),sQuery(id+"F0.wireOp",EDGE,"E20.filletArc"),sQuery(id+"F0.wireOp",EDGE,"E25.0"),sQuery(id+"F0.wireOp",EDGE,"E25.1"),sQuery(id+"F0.wireOp",EDGE,"E25.2"),sQuery(id+"F0.wireOp",EDGE,"E25.3"),sQuery(id+"F0.wireOp",EDGE,"E25.4"),sQuery(id+"F0.wireOp",EDGE,"E25.5"),sQuery(id+"F0.wireOp",EDGE,"E25.6"),sQuery(id+"F0.wireOp",EDGE,"E25.7")])],"isStart":false});
            extrude(context, id + "F17", {"entities" : qUnion([Q0, Q1, Q2]), "endBound" : BoundingType.UP_TO_SURFACE, "endBoundEntityFace" : qUnion([Q3]), "depth" : 25 * mm});
        }
    });
